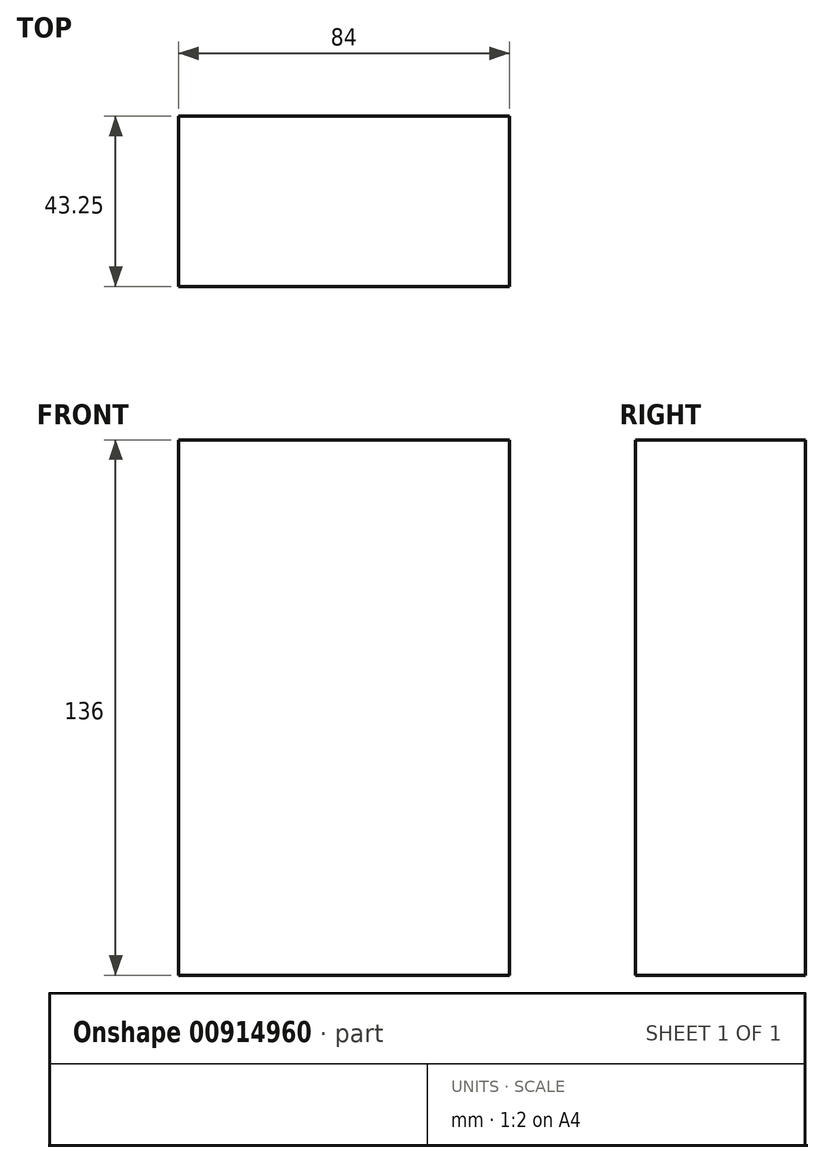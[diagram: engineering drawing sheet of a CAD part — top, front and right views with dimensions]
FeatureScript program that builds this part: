
annotation { "Feature Type Name" : "Feature", "Feature Type Description" : "" }
export const myFeature = defineFeature(function(context is Context, id is Id, definition is map)
    precondition{}
    {
        {
            var Q0;
            Q0=qCreatedBy(makeId("Front.planeOp"),FACE);
            var sketch = newSketch(context, id + "F0", { "sketchPlane" : qUnion([Q0])});
            skLineSegment(sketch, "E0.bottom", {"start": v(-44.26, 71.9) * mm, "end": v(39.74, 71.9) * mm});
            skLineSegment(sketch, "E0.top", {"start": v(-44.26, -64.1) * mm, "end": v(39.74, -64.1) * mm});
            skLineSegment(sketch, "E0.left", {"start": v(-44.26, 71.9) * mm, "end": v(-44.26, -64.1) * mm});
            skLineSegment(sketch, "E0.right", {"start": v(39.74, 71.9) * mm, "end": v(39.74, -64.1) * mm});
            skSolve(sketch);
        }
        {
            var Q0;
            Q0 = qSketchRegion(id + "F0", true);
            extrude(context, id + "F1", {"entities" : qUnion([Q0]), "depth" : 43.25 * mm, "offsetDistance" : 25 * mm});
        }
    });
